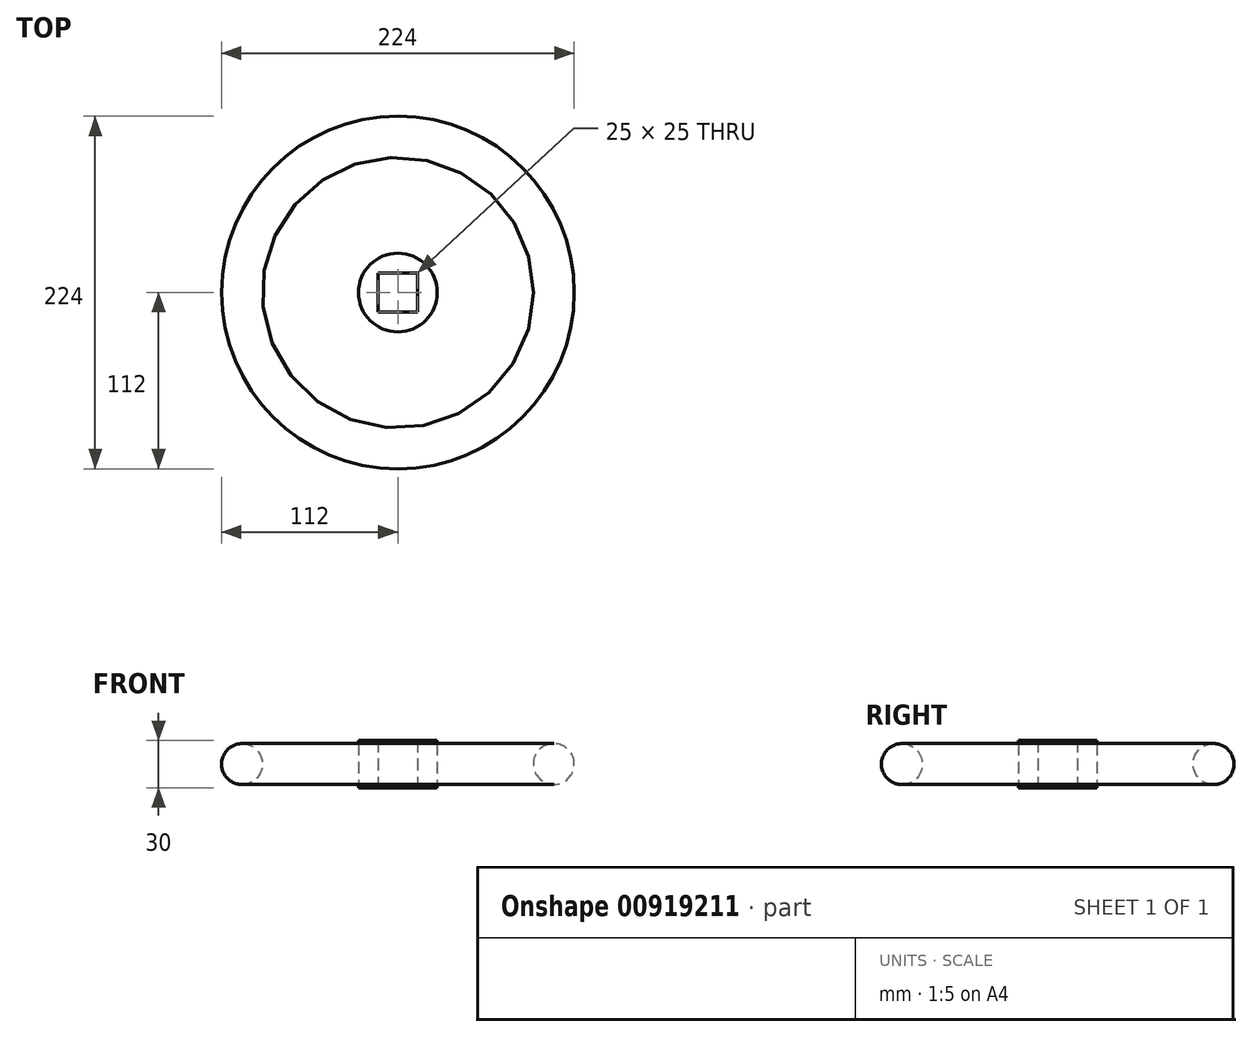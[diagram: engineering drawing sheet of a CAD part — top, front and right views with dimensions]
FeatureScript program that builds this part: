
annotation { "Feature Type Name" : "Feature", "Feature Type Description" : "" }
export const myFeature = defineFeature(function(context is Context, id is Id, definition is map)
    precondition{}
    {
        {
            var Q0;
            Q0=qCreatedBy(makeId("Front.planeOp"),FACE);
            var sketch = newSketch(context, id + "F0", { "sketchPlane" : qUnion([Q0])});
            skLineSegment(sketch, "E0", {"start": v(0, 78.54) * mm, "end": v(0, -92.17) * mm, "construction": true});
            skCircle(sketch, "E1", {"center": v(-99, 0) * mm, "radius": 13 * mm});
            skSolve(sketch);
        }
        {
            var Q0;
            Q0=makeQuery(id+"F0.imprint","IMPRINT",FACE,{"disambiguationData":[TD([[makeQuery(id+"F0.imprint","IMPRINT",EDGE,{"derivedFrom":sQuery(id+"F0.wireOp",EDGE,"E1")}),1.0]])]});
            var Q1;
            Q1=sQuery(id+"F0.wireOp",EDGE,"E0");
            revolve(context, id + "F1", {"surfaceOperationType" : NewSurfaceOperationType.NEW, "entities" : qUnion([Q0]), "axis" : qUnion([Q1]), "revolveType" : RevolveType.FULL});
        }
        {
            var Q0;
            Q0=qCreatedBy(makeId("Top.planeOp"),FACE);
            var sketch = newSketch(context, id + "F2", { "sketchPlane" : qUnion([Q0])});
            skCircle(sketch, "E2", {"center": v(0, 0) * mm, "radius": 25 * mm});
            skLineSegment(sketch, "E3.bottom", {"start": v(12.5, -12.5) * mm, "end": v(-12.5, -12.5) * mm});
            skLineSegment(sketch, "E3.top", {"start": v(12.5, 12.5) * mm, "end": v(-12.5, 12.5) * mm});
            skLineSegment(sketch, "E3.left", {"start": v(12.5, -12.5) * mm, "end": v(12.5, 12.5) * mm});
            skLineSegment(sketch, "E3.right", {"start": v(-12.5, -12.5) * mm, "end": v(-12.5, 12.5) * mm});
            skSolve(sketch);
        }
        {
            var Q0;
            Q0=makeQuery(id+"F2.imprint","IMPRINT",FACE,{"disambiguationData":[TD([[makeQuery(id+"F2.imprint","IMPRINT",EDGE,{"derivedFrom":sQuery(id+"F2.wireOp",EDGE,"E2")}),1.0]])]});
            extrude(context, id + "F3", {"entities" : qUnion([Q0]), "endBound" : BoundingType.SYMMETRIC, "depth" : 30 * mm, "offsetDistance" : 25 * mm});
        }
        {
            var Q0;
            Q0=qCreatedBy(makeId("Right.planeOp"),FACE);
            cPlane(context, id + "F4", {"entities" : qUnion([Q0]), "cplaneType" : CPlaneType.OFFSET, "offset" : 50 * mm, "oppositeDirection" : true, "width" : 150 * mm, "height" : 150 * mm});
        }
        {
            var Q0;
            Q0=qCreatedBy(id+"F4.planeOp",FACE);
            var sketch = newSketch(context, id + "F5", { "sketchPlane" : qUnion([Q0])});
            skEllipse(sketch, "E4", {"center": v(0, 0) * mm, "majorRadius": 10 * mm, "minorRadius": 5 * mm, "majorAxis": v(-1, 0)});
            skSolve(sketch);
        }
        {
            var Q0;
            Q0=sQuery(id+"F5.wireOp",EDGE,"E4");
            extrude(context, id + "F6", {"bodyType" : ToolBodyType.SURFACE, "surfaceEntities" : qUnion([Q0]), "endBound" : BoundingType.UP_TO_NEXT, "oppositeDirection" : true, "depth" : 25 * mm, "offsetDistance" : 25 * mm, "hasSecondDirection" : true, "secondDirectionBound" : SecondDirectionBoundingType.UP_TO_NEXT, "secondDirectionOppositeDirection" : false, "secondDirectionDepth" : 25 * mm});
        }
        {
            var Q0;
            Q0=makeQuery(id+"F6.opExtrude","SWEPT_BODY",BODY,{"disambiguationData":[OSD([sQuery(id+"F5.wireOp",EDGE,"E4")])]});
            var Q1;
            Q1=makeQuery(id+"F3.opExtrude","CAP_EDGE",EDGE,{"disambiguationData":[OSD([sQuery(id+"F2.wireOp",EDGE,"E2")])],"isStart":false});
            circularPattern(context, id + "F7", {"entities" : qUnion([Q0]), "axis" : qUnion([Q1]), "angle" : 360 * degree, "instanceCount" : 4, "equalSpace" : true});
        }
    });
